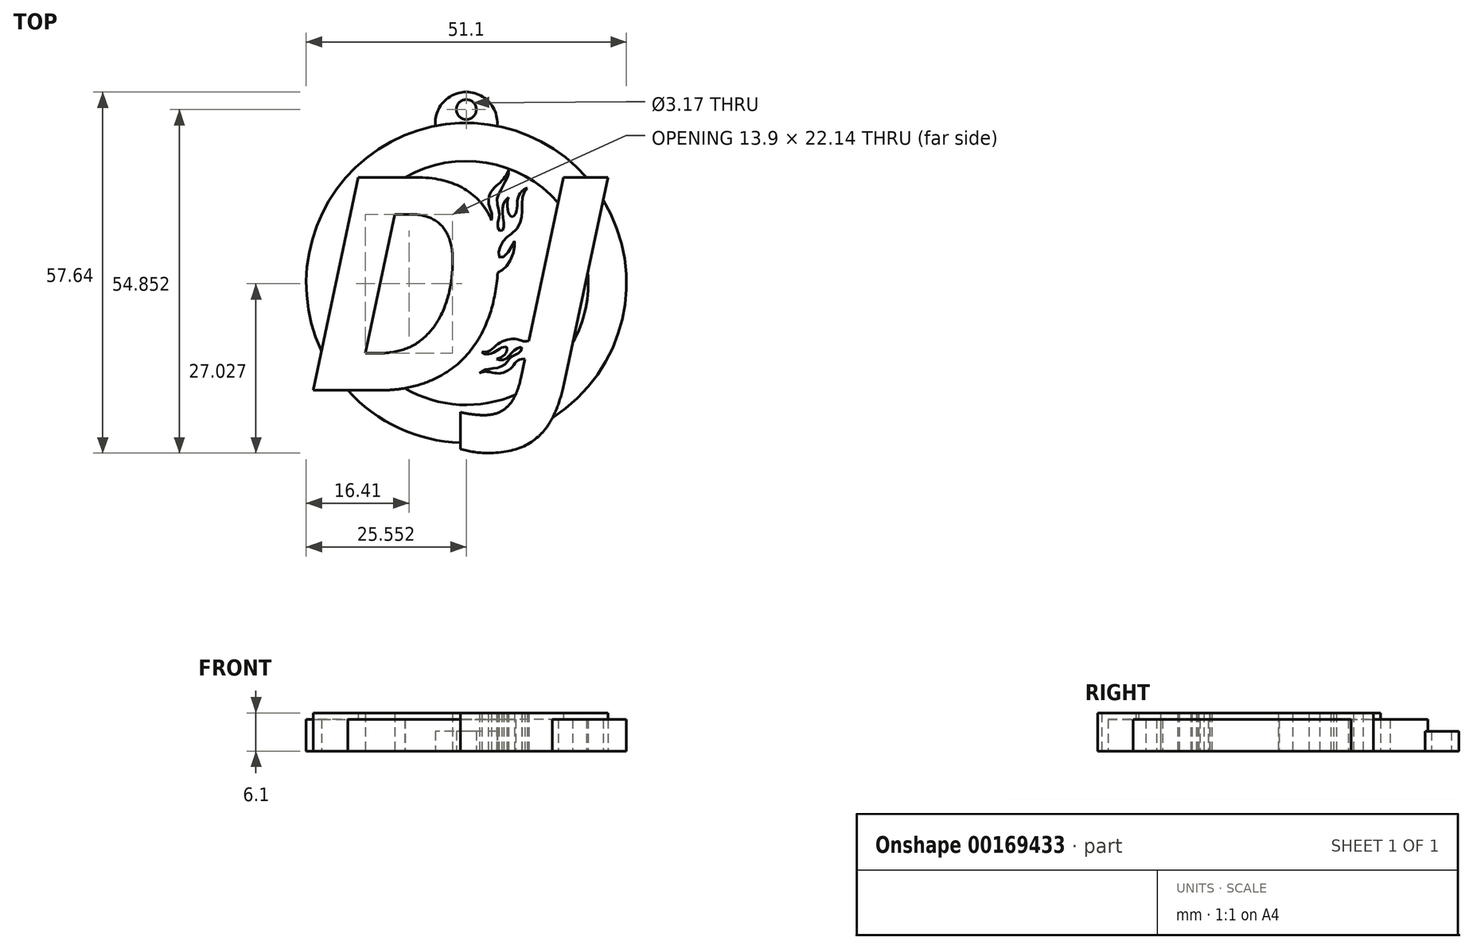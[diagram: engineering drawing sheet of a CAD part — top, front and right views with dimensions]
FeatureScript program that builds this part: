
annotation { "Feature Type Name" : "Feature", "Feature Type Description" : "" }
export const myFeature = defineFeature(function(context is Context, id is Id, definition is map)
    precondition{}
    {
        {
            var Q0;
            Q0=qCreatedBy(makeId("Top.planeOp"),FACE);
            var sketch = newSketch(context, id + "F0", { "sketchPlane" : qUnion([Q0])});
            skText(sketch, "E0", { "text": "DJ", "fontName": "OpenSans-BoldItalic.ttf"});
            skCircle(sketch, "E1", {"center": v(-21.05, 13.62) * mm, "radius": 25.55 * mm});
            skCircle(sketch, "E2", {"center": v(-21.05, 13.62) * mm, "radius": 19.47 * mm});
            skArc(sketch, "E3", {"start": v(-16.13, 38.69) * mm, "mid": v(-21.05, 44.11) * mm, "end": v(-25.97, 38.69) * mm});
            skCircle(sketch, "E4", {"center": v(-21.05, 41.32) * mm, "radius": 1.59 * mm});
            skFitSpline(sketch, "E5", {"points": [v(-17.02, 23.64) * mm, v(-16.98, 24.64) * mm, v(-17.38, 25.88) * mm, v(-17.45, 27.24) * mm, v(-16.85, 28.52) * mm, v(-15.83, 29.52) * mm, v(-14.9, 30.54) * mm, v(-14.32, 31.6) * mm], "startDerivative": vector(1.23, 7.85) * mm, "endDerivative": vector(3.67, 7.87) * mm});
            skFitSpline(sketch, "E6", {"points": [v(-14.32, 31.6) * mm, v(-14.32, 31) * mm, v(-14.68, 30.08) * mm, v(-15.36, 28.85) * mm, v(-15.8, 27.97) * mm, v(-16.15, 26.72) * mm, v(-15.85, 25.2) * mm, v(-15.8, 24.24) * mm, v(-16.03, 23.22) * mm, v(-15.86, 22.14) * mm, v(-15.47, 21.94) * mm, v(-15.12, 22.32) * mm, v(-15.04, 23.3) * mm, v(-15.26, 24.54) * mm, v(-15.27, 25.65) * mm, v(-14.95, 26.59) * mm, v(-14.32, 27.29) * mm], "startDerivative": vector(1.11, -11.9) * mm, "endDerivative": vector(11.38, 10.6) * mm});
            skFitSpline(sketch, "E7", {"points": [v(-14.32, 27.29) * mm, v(-14.49, 26.67) * mm, v(-14.49, 25.6) * mm, v(-14.16, 24.51) * mm, v(-13.67, 24.2) * mm, v(-13.14, 24.8) * mm, v(-12.9, 25.92) * mm, v(-12.86, 27) * mm, v(-12.45, 27.96) * mm, v(-11.66, 28.68) * mm, v(-11.33, 28.79) * mm], "startDerivative": vector(-2.3, -6.68) * mm, "endDerivative": vector(4.76, 0.83) * mm});
            skFitSpline(sketch, "E8", {"points": [v(-11.33, 28.79) * mm, v(-11.65, 28.41) * mm, v(-12.06, 27.54) * mm, v(-12.13, 26.43) * mm, v(-12.12, 25.02) * mm, v(-12.2, 24.2) * mm, v(-12.52, 23.14) * mm, v(-13.15, 22.1) * mm, v(-14.2, 21.23) * mm, v(-14.75, 20.84) * mm, v(-15.39, 19.94) * mm, v(-15.75, 19.12) * mm, v(-15.89, 18.34) * mm, v(-15.75, 17.71) * mm, v(-15.32, 17.7) * mm, v(-14.49, 18.4) * mm, v(-13.77, 19.5) * mm, v(-13.35, 20.23) * mm, v(-13.32, 19.83) * mm, v(-13.45, 18.77) * mm, v(-14.06, 17.14) * mm, v(-14.75, 16.22) * mm, v(-15.4, 15.65) * mm, v(-16.03, 15.27) * mm], "startDerivative": vector(-9.94, -10.26) * mm, "endDerivative": vector(-16.52, -8.94) * mm});
            skLineSegment(sketch, "E9", {"start": v(-17.02, 23.64) * mm, "end": v(-17.28, 22.87) * mm});
            skLineSegment(sketch, "E10", {"start": v(-17.28, 22.87) * mm, "end": v(-16.68, 16.1) * mm});
            skLineSegment(sketch, "E11", {"start": v(-16.68, 16.1) * mm, "end": v(-16.03, 15.27) * mm});
            skFitSpline(sketch, "E12", {"points": [v(-11.13, 4.38) * mm, v(-11.8, 4.3) * mm, v(-12.5, 4.51) * mm, v(-13.44, 4.68) * mm, v(-14.14, 4.65) * mm, v(-15.54, 4.16) * mm, v(-16.6, 3.35) * mm, v(-17.53, 2.7) * mm, v(-18.55, 2.6) * mm], "startDerivative": vector(-6.63, -1.59) * mm, "endDerivative": vector(-8.24, 0.36) * mm});
            skFitSpline(sketch, "E13", {"points": [v(-18.55, 2.6) * mm, v(-17.94, 2.23) * mm, v(-16.52, 2.6) * mm, v(-15.44, 3.26) * mm, v(-14.64, 3.38) * mm, v(-14.52, 3.04) * mm, v(-14.85, 2.3) * mm, v(-15.62, 1.71) * mm, v(-16.18, 1.47) * mm], "startDerivative": vector(4.44, -4.3) * mm, "endDerivative": vector(-4.99, -1.85) * mm});
            skFitSpline(sketch, "E14", {"points": [v(-16.18, 1.47) * mm, v(-15.49, 1.3) * mm, v(-14.4, 1.76) * mm, v(-13.7, 2.6) * mm, v(-12.84, 3.21) * mm, v(-12.26, 3.37) * mm, v(-12.24, 2.9) * mm, v(-13.02, 2.22) * mm, v(-13.9, 1.83) * mm, v(-14.52, 1) * mm, v(-15.56, 0.24) * mm, v(-17.08, -0.06) * mm, v(-18.14, -0.27) * mm, v(-18.95, -0.74) * mm], "startDerivative": vector(9.7, -4.11) * mm, "endDerivative": vector(-10.36, -7.21) * mm});
            skFitSpline(sketch, "E15", {"points": [v(-18.95, -0.74) * mm, v(-17.94, -0.54) * mm, v(-16.59, -0.74) * mm, v(-15.32, -0.74) * mm, v(-13.83, 0.07) * mm, v(-12.99, 1.15) * mm, v(-12.16, 1.47) * mm, v(-11.48, 1.47) * mm], "startDerivative": vector(7.19, 2.24) * mm, "endDerivative": vector(5.98, -0.36) * mm});
            skLineSegment(sketch, "E16", {"start": v(-11.13, 4.38) * mm, "end": v(-10.47, 4.38) * mm});
            skLineSegment(sketch, "E17", {"start": v(-10.47, 4.38) * mm, "end": v(-11.48, 1.47) * mm});
            const initialGuessF0  = {"E0": [-0.04673, -0.00353, 1, 0, 0.0343]};
            skSetInitialGuess(sketch, initialGuessF0);
            skSolve(sketch);
        }
        {
            var Q0;
            Q0=makeQuery(id+"F0.imprint","IMPRINT",FACE,{"disambiguationData":[TD([[makeQuery(id+"F0.imprint","IMPRINT",EDGE,{"derivedFrom":sQuery(id+"F0.wireOp",EDGE,"E0.sketch_text.stroke-0")}),-1.0]])]});
            var Q1;
            {var subQ5=sQuery(id+"F0.wireOp",EDGE,"E0.sketch_text.stroke-2");var subQ11=sQuery(id+"F0.wireOp",EDGE,"E0.sketch_text.stroke-3");var subQ12=makeQuery(id+"F0.imprint","INTERSECT",VERTEX,{"derivedFrom":[subQ5,subQ11]});Q1=makeQuery(id+"F0.imprint","IMPRINT",FACE,{"disambiguationData":[TD([[makeQuery(id+"F0.imprint","IMPRINT",EDGE,{"disambiguationData":[TD([[subQ12,1.0]])],"derivedFrom":subQ5}),-1.0]])]});}
            var Q2;
            {var subQ1=sQuery(id+"F0.wireOp",EDGE,"E0.sketch_text.stroke-21");var subQ6=sQuery(id+"F0.wireOp",EDGE,"E0.sketch_text.stroke-20");var subQ7=makeQuery(id+"F0.imprint","INTERSECT",VERTEX,{"derivedFrom":[subQ6,subQ1]});Q2=makeQuery(id+"F0.imprint","IMPRINT",FACE,{"disambiguationData":[TD([[makeQuery(id+"F0.imprint","IMPRINT",EDGE,{"disambiguationData":[TD([[subQ7,1.0]])],"derivedFrom":subQ6}),-1.0]])]});}
            var Q3;
            {var subQ1=sQuery(id+"F0.wireOp",EDGE,"E0.sketch_text.stroke-22");var subQ7=sQuery(id+"F0.wireOp",EDGE,"E0.sketch_text.stroke-21");var subQ8=makeQuery(id+"F0.imprint","INTERSECT",VERTEX,{"derivedFrom":[subQ7,subQ1]});Q3=makeQuery(id+"F0.imprint","IMPRINT",FACE,{"disambiguationData":[TD([[makeQuery(id+"F0.imprint","IMPRINT",EDGE,{"disambiguationData":[TD([[subQ8,1.0]])],"derivedFrom":subQ7}),-1.0]])]});}
            var Q4;
            {var subQ0=sQuery(id+"F0.wireOp",EDGE,"E0.sketch_text.stroke-23");var subQ1=sQuery(id+"F0.wireOp",EDGE,"E0.sketch_text.stroke-22");var subQ2=makeQuery(id+"F0.imprint","INTERSECT",VERTEX,{"derivedFrom":[subQ1,subQ0]});Q4=makeQuery(id+"F0.imprint","IMPRINT",FACE,{"disambiguationData":[TD([[makeQuery(id+"F0.imprint","IMPRINT",EDGE,{"disambiguationData":[TD([[subQ2,1.0]])],"derivedFrom":subQ1}),-1.0]])]});}
            var Q5;
            {var subQ4=sQuery(id+"F0.wireOp",EDGE,"E0.sketch_text.stroke-18");Q5=makeQuery(id+"F0.imprint","IMPRINT",FACE,{"disambiguationData":[TD([[makeQuery(id+"F0.imprint","IMPRINT",EDGE,{"derivedFrom":subQ4}),-1.0]])]});}
            var Q6;
            {var subQ5=sQuery(id+"F0.wireOp",EDGE,"E0.sketch_text.stroke-16");Q6=makeQuery(id+"F0.imprint","IMPRINT",FACE,{"disambiguationData":[TD([[makeQuery(id+"F0.imprint","IMPRINT",EDGE,{"derivedFrom":subQ5}),-1.0]])]});}
            var Q7;
            {var subQ0=sQuery(id+"F0.wireOp",EDGE,"E0.sketch_text.stroke-4");var subQ1=sQuery(id+"F0.wireOp",EDGE,"E0.sketch_text.stroke-3");var subQ2=makeQuery(id+"F0.imprint","INTERSECT",VERTEX,{"derivedFrom":[subQ1,subQ0]});Q7=makeQuery(id+"F0.imprint","IMPRINT",FACE,{"disambiguationData":[TD([[makeQuery(id+"F0.imprint","IMPRINT",EDGE,{"disambiguationData":[TD([[subQ2,1.0]])],"derivedFrom":subQ1}),-1.0]])]});}
            var Q8;
            {var subQ9=sQuery(id+"F0.wireOp",EDGE,"E0.sketch_text.stroke-1");Q8=makeQuery(id+"F0.imprint","IMPRINT",FACE,{"disambiguationData":[TD([[makeQuery(id+"F0.imprint","IMPRINT",EDGE,{"derivedFrom":subQ9}),-1.0]])]});}
            extrude(context, id + "F1", {"entities" : qUnion([Q0, Q1, Q2, Q3, Q4, Q5, Q6, Q7, Q8]), "depth" : 6.1 * mm});
        }
        {
            var Q0;
            {var subQ9=sQuery(id+"F0.wireOp",EDGE,"E0.sketch_text.stroke-5");var subQ10=sQuery(id+"F0.wireOp",EDGE,"E0.sketch_text.stroke-4");var subQ11=makeQuery(id+"F0.imprint","INTERSECT",VERTEX,{"derivedFrom":[subQ10,subQ9]});Q0=makeQuery(id+"F0.imprint","IMPRINT",FACE,{"disambiguationData":[TD([[makeQuery(id+"F0.imprint","IMPRINT",EDGE,{"disambiguationData":[TD([[subQ11,1.0]])],"derivedFrom":subQ10}),1.0]])]});}
            var Q1;
            {var subQ0=sQuery(id+"F0.wireOp",EDGE,"E1");var subQ1=sQuery(id+"F0.wireOp",EDGE,"E0.sketch_text.stroke-23");var subQ2=makeQuery(id+"F0.imprint","INTERSECT",VERTEX,{"derivedFrom":[subQ1,subQ0]});Q1=makeQuery(id+"F0.imprint","IMPRINT",FACE,{"disambiguationData":[TD([[makeQuery(id+"F0.imprint","IMPRINT",EDGE,{"disambiguationData":[TD([[subQ2,-1.0]])],"derivedFrom":subQ1}),1.0]])]});}
            var Q2;
            {var subQ0=sQuery(id+"F0.wireOp",EDGE,"E0.sketch_text.stroke-18");Q2=makeQuery(id+"F0.imprint","IMPRINT",FACE,{"disambiguationData":[TD([[makeQuery(id+"F0.imprint","IMPRINT",EDGE,{"derivedFrom":subQ0}),1.0]])]});}
            extrude(context, id + "F2", {"entities" : qUnion([Q0, Q1, Q2]), "operationType" : NewBodyOperationType.ADD, "depth" : 5.08 * mm});
        }
        {
            var Q0;
            {var subQ4=sQuery(id+"F0.wireOp",EDGE,"E5");Q0=makeQuery(id+"F0.imprint","IMPRINT",FACE,{"disambiguationData":[TD([[makeQuery(id+"F0.imprint","IMPRINT",EDGE,{"derivedFrom":subQ4}),-1.0]])]});}
            extrude(context, id + "F3", {"entities" : qUnion([Q0]), "operationType" : NewBodyOperationType.ADD, "depth" : 6.1 * mm});
        }
        {
            var Q0;
            {var subQ1=sQuery(id+"F0.wireOp",EDGE,"E12");Q0=makeQuery(id+"F0.imprint","IMPRINT",FACE,{"disambiguationData":[TD([[makeQuery(id+"F0.imprint","IMPRINT",EDGE,{"derivedFrom":subQ1}),1.0]])]});}
            var Q1;
            {var subQ5=sQuery(id+"F0.wireOp",EDGE,"E17");Q1=makeQuery(id+"F0.imprint","IMPRINT",FACE,{"disambiguationData":[TD([[makeQuery(id+"F0.imprint","IMPRINT",EDGE,{"derivedFrom":subQ5}),-1.0]])]});}
            extrude(context, id + "F4", {"entities" : qUnion([Q0, Q1]), "operationType" : NewBodyOperationType.ADD, "depth" : 6.1 * mm});
        }
        {
            var Q0;
            {var subQ0=sQuery(id+"F0.wireOp",EDGE,"E3");Q0=makeQuery(id+"F0.imprint","IMPRINT",FACE,{"disambiguationData":[TD([[makeQuery(id+"F0.imprint","IMPRINT",EDGE,{"derivedFrom":subQ0}),1.0]])]});}
            extrude(context, id + "F5", {"entities" : qUnion([Q0]), "operationType" : NewBodyOperationType.ADD, "depth" : 3.17 * mm});
        }
    });
